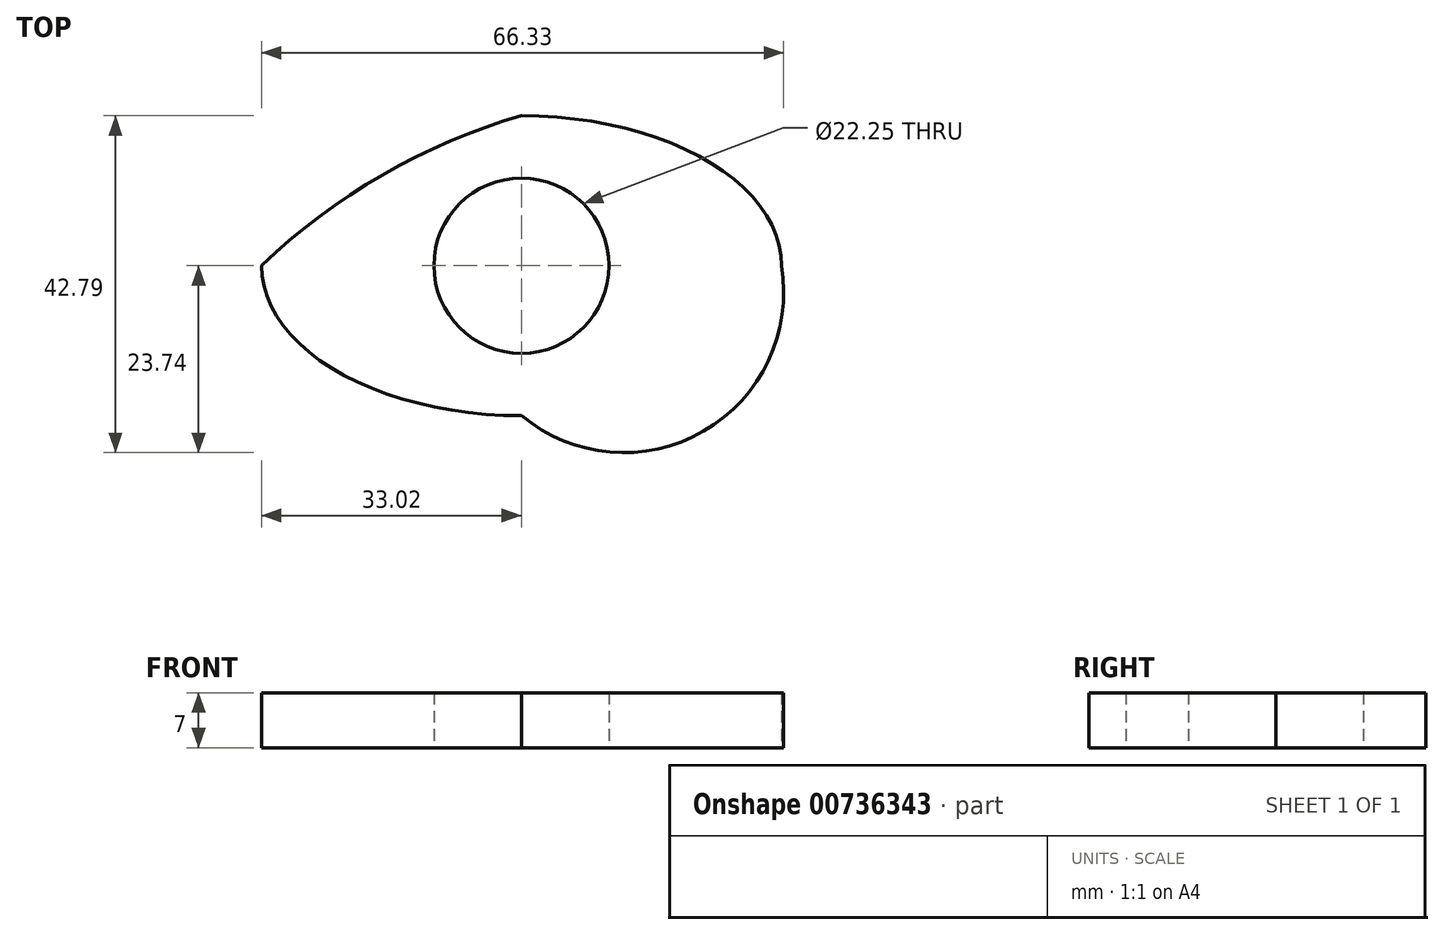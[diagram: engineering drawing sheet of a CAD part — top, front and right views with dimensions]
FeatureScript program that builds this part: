
annotation { "Feature Type Name" : "Feature", "Feature Type Description" : "" }
export const myFeature = defineFeature(function(context is Context, id is Id, definition is map)
    precondition{}
    {
        {
            var Q0;
            Q0=qCreatedBy(makeId("Top.planeOp"),FACE);
            var sketch = newSketch(context, id + "F0", { "sketchPlane" : qUnion([Q0])});
            skEllipse(sketch, "E0", {"center": v(0, 0) * mm, "majorRadius": 33.02 * mm, "minorRadius": 19.05 * mm, "majorAxis": v(1, 0)});
            skCircle(sketch, "E1", {"center": v(0, 0) * mm, "radius": 11.12 * mm});
            skLineSegment(sketch, "E2", {"start": v(-33.02, 0) * mm, "end": v(33.02, 0) * mm, "construction": true});
            skLineSegment(sketch, "E3", {"start": v(0, 19.05) * mm, "end": v(0, -19.05) * mm, "construction": true});
            skArc(sketch, "E4", {"start": v(0, 19.05) * mm, "mid": v(-17.66, 11.52) * mm, "end": v(-33.02, 0) * mm});
            skArc(sketch, "E5", {"start": v(0, -19.05) * mm, "mid": v(23.15, -21.03) * mm, "end": v(33.02, 0) * mm});
            skSolve(sketch);
        }
        {
            var Q0;
            {var subQ0=sQuery(id+"F0.wireOp",EDGE,"E4");Q0=makeQuery(id+"F0.imprint","IMPRINT",FACE,{"disambiguationData":[TD([[makeQuery(id+"F0.imprint","IMPRINT",EDGE,{"derivedFrom":subQ0}),1.0]])]});}
            var Q1;
            Q1=makeQuery(id+"F0.imprint","IMPRINT",FACE,{"disambiguationData":[TD([[makeQuery(id+"F0.imprint","IMPRINT",EDGE,{"derivedFrom":sQuery(id+"F0.wireOp",EDGE,"E1")}),-1.0]])]});
            var Q2;
            {var subQ0=sQuery(id+"F0.wireOp",EDGE,"E5");Q2=makeQuery(id+"F0.imprint","IMPRINT",FACE,{"disambiguationData":[TD([[makeQuery(id+"F0.imprint","IMPRINT",EDGE,{"derivedFrom":subQ0}),1.0]])]});}
            extrude(context, id + "F1", {"entities" : qUnion([Q0, Q1, Q2]), "depth" : 7 * mm, "offsetDistance" : 25.4 * mm});
        }
    });
